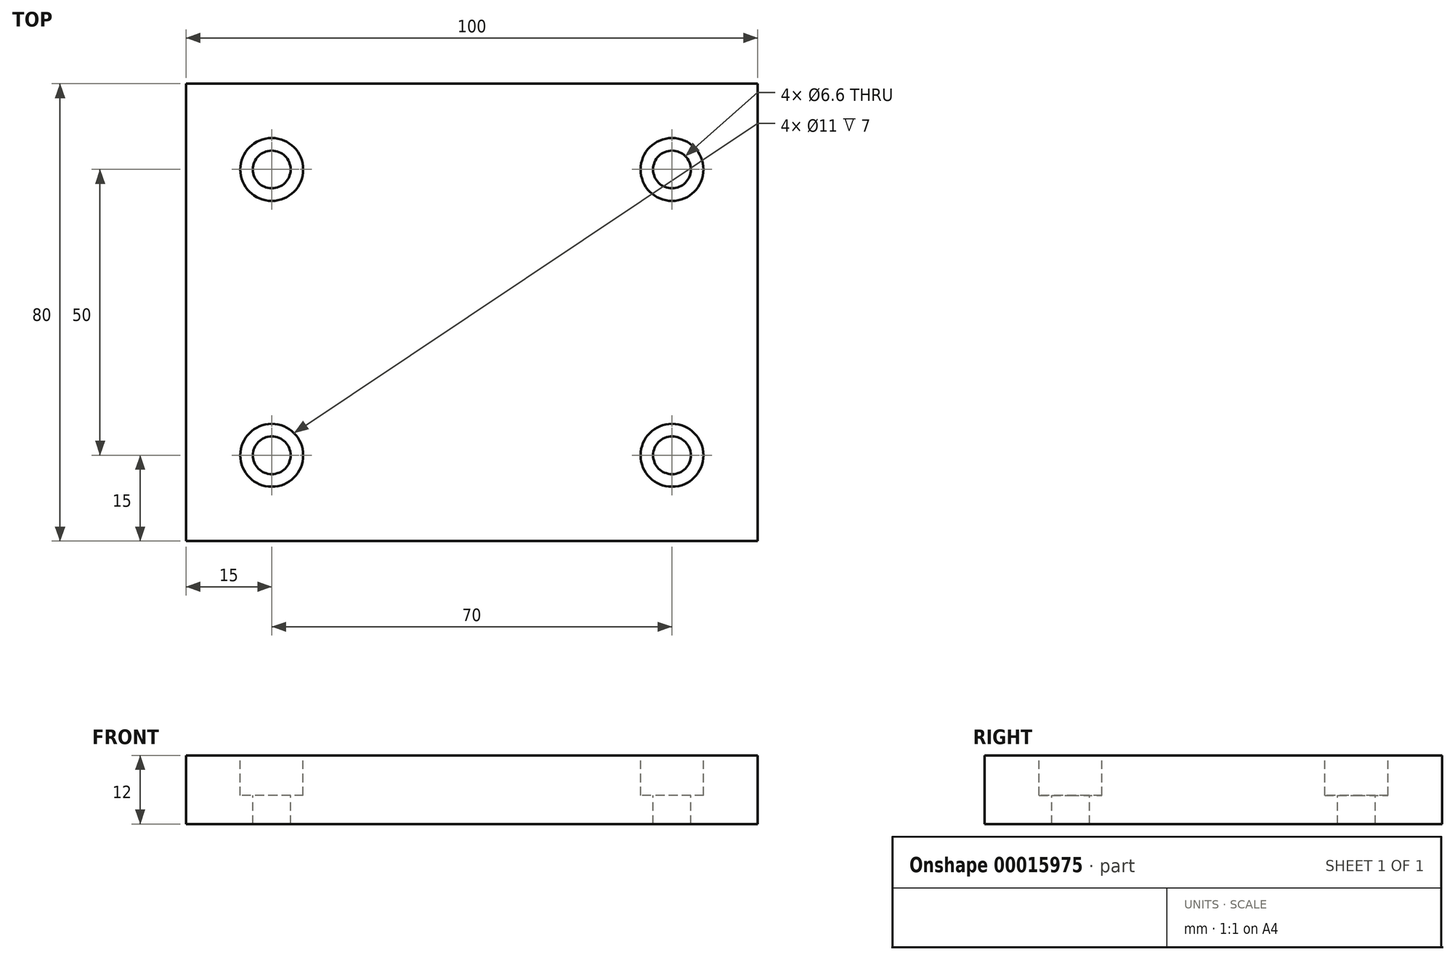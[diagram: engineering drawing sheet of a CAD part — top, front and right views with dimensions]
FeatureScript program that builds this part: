
annotation { "Feature Type Name" : "Feature", "Feature Type Description" : "" }
export const myFeature = defineFeature(function(context is Context, id is Id, definition is map)
    precondition{}
    {
        {
            var Q0;
            Q0=qCreatedBy(makeId("Top.planeOp"),FACE);
            var sketch = newSketch(context, id + "F0", { "sketchPlane" : qUnion([Q0])});
            skLineSegment(sketch, "E0.rect.bottom", {"start": v(50, 40) * mm, "end": v(-50, 40) * mm});
            skLineSegment(sketch, "E0.rect.top", {"start": v(50, -40) * mm, "end": v(-50, -40) * mm});
            skLineSegment(sketch, "E0.rect.left", {"start": v(50, 40) * mm, "end": v(50, -40) * mm});
            skLineSegment(sketch, "E0.rect.right", {"start": v(-50, 40) * mm, "end": v(-50, -40) * mm});
            skPoint(sketch, "E0.rect.middle", {"position": v(0, 0) * mm});
            skSolve(sketch);
        }
        {
            var Q0;
            Q0=makeQuery(id+"F0.imprint","IMPRINT",FACE,{"disambiguationData":[TD([[makeQuery(id+"F0.imprint","IMPRINT",EDGE,{"derivedFrom":sQuery(id+"F0.wireOp",EDGE,"E0.rect.bottom")}),1.0]])]});
            extrude(context, id + "F1", {"entities" : qUnion([Q0]), "depth" : 12 * mm});
        }
        {
            var Q0;
            Q0=makeQuery(id+"F1.opExtrude","CAP_FACE",FACE,{"disambiguationData":[OSD([sQuery(id+"F0.wireOp",EDGE,"E0.rect.bottom"),sQuery(id+"F0.wireOp",EDGE,"E0.rect.top"),sQuery(id+"F0.wireOp",EDGE,"E0.rect.left"),sQuery(id+"F0.wireOp",EDGE,"E0.rect.right")])],"isStart":false});
            var sketch = newSketch(context, id + "F2", { "sketchPlane" : qUnion([Q0])});
            skLineSegment(sketch, "E1.rect.bottom", {"start": v(35, 25) * mm, "end": v(-35, 25) * mm});
            skLineSegment(sketch, "E1.rect.top", {"start": v(35, -25) * mm, "end": v(-35, -25) * mm});
            skLineSegment(sketch, "E1.rect.left", {"start": v(35, 25) * mm, "end": v(35, -25) * mm});
            skLineSegment(sketch, "E1.rect.right", {"start": v(-35, 25) * mm, "end": v(-35, -25) * mm});
            skPoint(sketch, "E1.rect.middle", {"position": v(0, 0) * mm});
            skSolve(sketch);
        }
        {
            var Q0;
            Q0=sQuery(id+"F2.wireOp",VERTEX,"E1.rect.right.start");
            var Q1;
            Q1=sQuery(id+"F2.wireOp",VERTEX,"E1.rect.bottom.start");
            var Q2;
            Q2=sQuery(id+"F2.wireOp",VERTEX,"E1.rect.left.end");
            var Q3;
            Q3=sQuery(id+"F2.wireOp",VERTEX,"E1.rect.top.end");
            var Q4;
            Q4=makeQuery(id+"F1.opExtrude","SWEPT_BODY",BODY,{"disambiguationData":[OSD([sQuery(id+"F0.wireOp",EDGE,"E0.rect.bottom"),sQuery(id+"F0.wireOp",EDGE,"E0.rect.top"),sQuery(id+"F0.wireOp",EDGE,"E0.rect.left"),sQuery(id+"F0.wireOp",EDGE,"E0.rect.right")])]});
            hole(context, id + "F3", {"style" : HoleStyle.C_BORE, "holeDiameter" : 6.6 * mm, "cBoreDiameter" : 11 * mm, "cBoreDepth" : 7 * mm, "endStyle" : HoleEndStyle.THROUGH, "locations" : qUnion([Q0, Q1, Q2, Q3]), "scope" : qUnion([Q4])});
        }
    });
